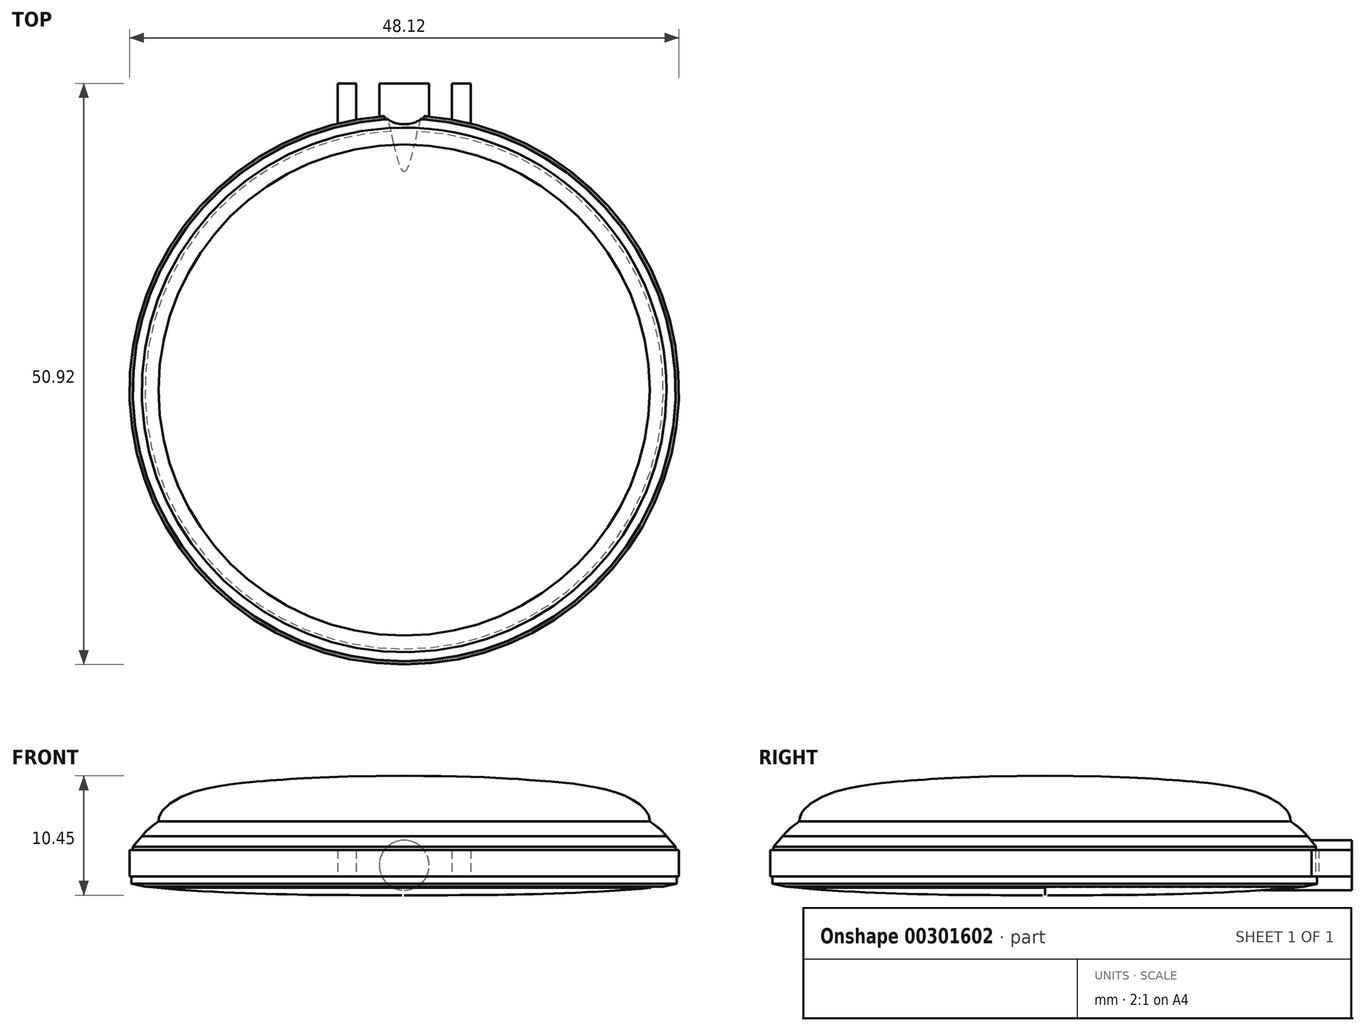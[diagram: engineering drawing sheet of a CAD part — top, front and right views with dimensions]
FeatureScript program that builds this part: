
annotation { "Feature Type Name" : "Feature", "Feature Type Description" : "" }
export const myFeature = defineFeature(function(context is Context, id is Id, definition is map)
    precondition{}
    {
        {
            var Q0;
            Q0=qCreatedBy(makeId("Top.planeOp"),FACE);
            var sketch = newSketch(context, id + "F0", { "sketchPlane" : qUnion([Q0])});
            skCircle(sketch, "E0", {"center": v(0, 0) * mm, "radius": 24.06 * mm});
            skSolve(sketch);
        }
        {
            var Q0;
            Q0=qSketchRegion(id+"F0",true);
            extrude(context, id + "F1", {"entities" : qUnion([Q0]), "depth" : 2.32 * mm});
        }
        {
            var Q0;
            Q0=qCreatedBy(makeId("Front.planeOp"),FACE);
            var sketch = newSketch(context, id + "F2", { "sketchPlane" : qUnion([Q0])});
            skLineSegment(sketch, "E1", {"start": v(0, 66.42) * mm, "end": v(0, -62.07) * mm, "construction": true});
            skFitSpline(sketch, "E2", {"points": [v(0, -1.65) * mm, v(10.95, -1.56) * mm, v(21.63, -1) * mm], "startDerivative": vector(34.83, 0) * mm, "endDerivative": vector(19.05, 1.97) * mm});
            skLineSegment(sketch, "E3", {"start": v(23.88, 0) * mm, "end": v(23.88, -0.66) * mm});
            skLineSegment(sketch, "E4", {"start": v(23.88, -0.66) * mm, "end": v(22.7, -0.9) * mm});
            skLineSegment(sketch, "E5", {"start": v(22.7, -0.9) * mm, "end": v(21.63, -1) * mm});
            skLineSegment(sketch, "E6", {"start": v(0, -1.65) * mm, "end": v(0, 0) * mm});
            skLineSegment(sketch, "E7", {"start": v(0, 0) * mm, "end": v(23.88, 0) * mm});
            skSolve(sketch);
        }
        {
            var Q0;
            Q0=qSketchRegion(id+"F2",true);
            var Q1;
            Q1=sQuery(id+"F2.wireOp",EDGE,"E1");
            revolve(context, id + "F3", {"operationType" : NewBodyOperationType.ADD, "entities" : qUnion([Q0]), "axis" : qUnion([Q1]), "revolveType" : RevolveType.FULL});
        }
        {
            var Q0;
            Q0=qCreatedBy(makeId("Front.planeOp"),FACE);
            var sketch = newSketch(context, id + "F4", { "sketchPlane" : qUnion([Q0])});
            skLineSegment(sketch, "E8", {"start": v(23.77, 2.32) * mm, "end": v(23.77, 2.6) * mm});
            skLineSegment(sketch, "E9", {"start": v(23.77, 2.6) * mm, "end": v(22.98, 3.5) * mm});
            skLineSegment(sketch, "E10", {"start": v(22.98, 3.5) * mm, "end": v(22.98, 3.74) * mm});
            skLineSegment(sketch, "E11", {"start": v(22.98, 3.74) * mm, "end": v(21.5, 4.82) * mm});
            skLineSegment(sketch, "E12", {"start": v(21.5, 4.82) * mm, "end": v(0, 4.82) * mm});
            skLineSegment(sketch, "E13", {"start": v(0, 4.82) * mm, "end": v(0, 2.32) * mm});
            skLineSegment(sketch, "E14", {"start": v(0, 2.32) * mm, "end": v(23.77, 2.32) * mm});
            skSolve(sketch);
        }
        {
            var Q0;
            Q0=qSketchRegion(id+"F4",true);
            var Q1;
            Q1=sQuery(id+"F2.wireOp",EDGE,"E1");
            revolve(context, id + "F5", {"operationType" : NewBodyOperationType.ADD, "entities" : qUnion([Q0]), "axis" : qUnion([Q1]), "revolveType" : RevolveType.FULL});
        }
        {
            var Q0;
            Q0=qCreatedBy(makeId("Front.planeOp"),FACE);
            var sketch = newSketch(context, id + "F6", { "sketchPlane" : qUnion([Q0])});
            skFitSpline(sketch, "E15", {"points": [v(21.51, 4.82) * mm, v(19.12, 7.14) * mm, v(11.78, 8.39) * mm, v(0, 8.8) * mm], "startDerivative": vector(0, 12.59) * mm, "endDerivative": vector(-41.08, 0) * mm});
            skLineSegment(sketch, "E16", {"start": v(0, 8.8) * mm, "end": v(0, 4.82) * mm});
            skLineSegment(sketch, "E17", {"start": v(0, 4.82) * mm, "end": v(21.51, 4.82) * mm});
            skSolve(sketch);
        }
        {
            var Q0;
            Q0=qSketchRegion(id+"F6",true);
            var Q1;
            Q1=sQuery(id+"F2.wireOp",EDGE,"E1");
            revolve(context, id + "F7", {"operationType" : NewBodyOperationType.ADD, "entities" : qUnion([Q0]), "axis" : qUnion([Q1]), "revolveType" : RevolveType.FULL});
        }
        {
            var Q0;
            Q0=qCreatedBy(makeId("Top.planeOp"),FACE);
            var sketch = newSketch(context, id + "F8", { "sketchPlane" : qUnion([Q0])});
            skLineSegment(sketch, "E18", {"start": v(0, 37.72) * mm, "end": v(0, 2.03) * mm, "construction": true});
            skLineSegment(sketch, "E19", {"start": v(4.2, 23.69) * mm, "end": v(4.2, 26.86) * mm});
            skLineSegment(sketch, "E20", {"start": v(4.2, 26.86) * mm, "end": v(5.82, 26.86) * mm});
            skLineSegment(sketch, "E21", {"start": v(5.82, 26.86) * mm, "end": v(5.82, 23.34) * mm});
            skLineSegment(sketch, "E22", {"start": v(5.82, 23.34) * mm, "end": v(4.96, 22.06) * mm});
            skLineSegment(sketch, "E23", {"start": v(4.96, 22.06) * mm, "end": v(4.2, 23.69) * mm});
            skLineSegment(sketch, "E24.MirrorCS", {"start": v(-5.82, 23.34) * mm, "end": v(-4.96, 22.06) * mm});
            skLineSegment(sketch, "E25.MirrorCS", {"start": v(-5.82, 26.86) * mm, "end": v(-5.82, 23.34) * mm});
            skLineSegment(sketch, "E26.MirrorCS", {"start": v(-4.96, 22.06) * mm, "end": v(-4.19, 23.69) * mm});
            skLineSegment(sketch, "E27.MirrorCS", {"start": v(-4.19, 23.69) * mm, "end": v(-4.19, 26.86) * mm});
            skLineSegment(sketch, "E28.MirrorCS", {"start": v(-4.19, 26.86) * mm, "end": v(-5.82, 26.86) * mm});
            skCircle(sketch, "E29.0.0", {"center": v(0, 0) * mm, "radius": 24.06 * mm, "construction": true});
            skSolve(sketch);
        }
        {
            var Q0;
            Q0=qSketchRegion(id+"F8",true);
            extrude(context, id + "F9", {"entities" : qUnion([Q0]), "operationType" : NewBodyOperationType.ADD, "depth" : 2.3 * mm});
        }
        {
            var Q0;
            Q0=qCreatedBy(makeId("Front.planeOp"),FACE);
            var sketch = newSketch(context, id + "F10", { "sketchPlane" : qUnion([Q0])});
            skLineSegment(sketch, "E30", {"start": v(0, 0) * mm, "end": v(0, 17.8) * mm, "construction": true});
            skCircle(sketch, "E31", {"center": v(0, 0.97) * mm, "radius": 2.19 * mm});
            skSolve(sketch);
        }
        {
            var Q0;
            Q0=qSketchRegion(id+"F10",true);
            extrude(context, id + "F11", {"entities" : qUnion([Q0]), "operationType" : NewBodyOperationType.ADD, "oppositeDirection" : true, "depth" : 26.86 * mm});
        }
        {
            var Q0;
            Q0=makeQuery(id+"F5.opRevolve","SWEPT_FACE",FACE,{"disambiguationData":[OSD([sQuery(id+"F4.wireOp",EDGE,"E11")])]});
            fillet(context, id + "F12", {"entities" : qUnion([Q0]), "radius" : 5 * mm, "tangentPropagation" : true, "allowEdgeOverflow" : false});
        }
    });
